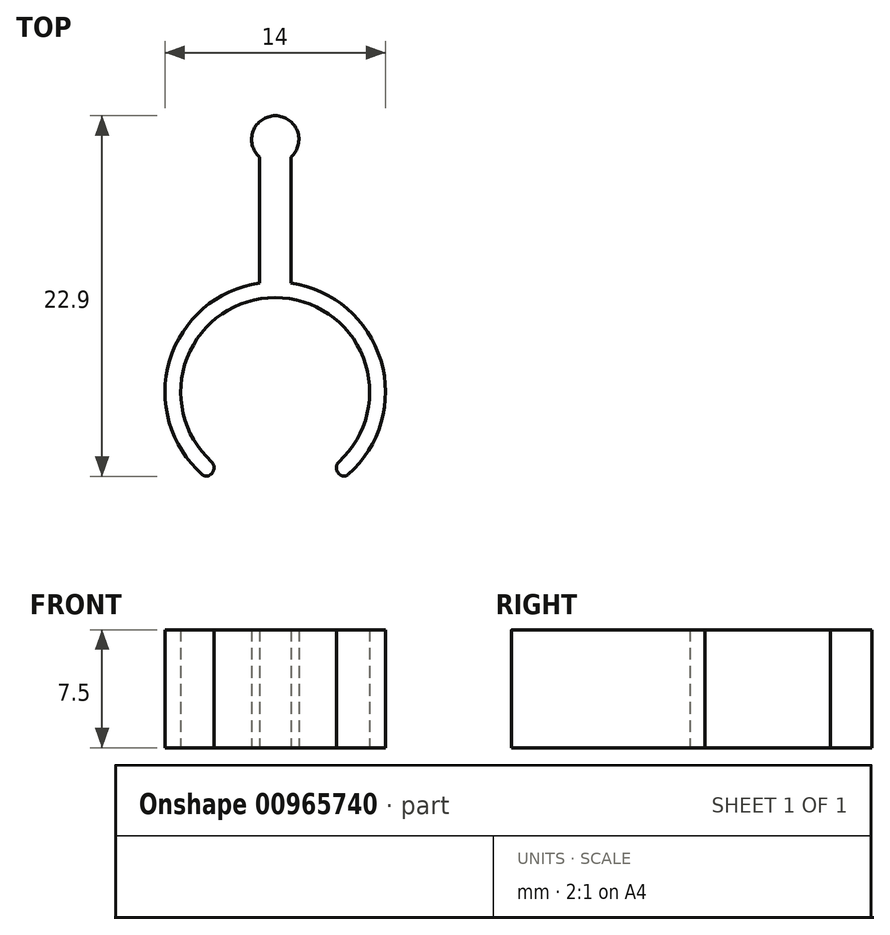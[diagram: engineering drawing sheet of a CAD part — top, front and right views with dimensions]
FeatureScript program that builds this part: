
annotation { "Feature Type Name" : "Feature", "Feature Type Description" : "" }
export const myFeature = defineFeature(function(context is Context, id is Id, definition is map)
    precondition{}
    {
        {
            var Q0;
            Q0=qCreatedBy(makeId("Top.planeOp"),FACE);
            var sketch = newSketch(context, id + "F0", { "sketchPlane" : qUnion([Q0])});
            skArc(sketch, "E0", {"start": v(4.64, -5.24) * mm, "mid": v(6.7, 2) * mm, "end": v(1, 6.93) * mm});
            skArc(sketch, "E1", {"start": v(4.05, -4.43) * mm, "mid": v(0, 6) * mm, "end": v(-4.05, -4.43) * mm});
            skLineSegment(sketch, "E2", {"start": v(3.99, -5.1) * mm, "end": v(4.06, -5.2) * mm});
            skLineSegment(sketch, "E3", {"start": v(-3.99, -5.1) * mm, "end": v(-4.06, -5.2) * mm});
            skLineSegment(sketch, "E4.left", {"start": v(1, 14.93) * mm, "end": v(1, 6.93) * mm});
            skLineSegment(sketch, "E4.right", {"start": v(-1, 14.93) * mm, "end": v(-1, 6.93) * mm});
            skArc(sketch, "E5.trimOffspring", {"start": v(-1, 6.93) * mm, "mid": v(-6.7, 2) * mm, "end": v(-4.64, -5.24) * mm});
            skArc(sketch, "E6", {"start": v(1, 14.93) * mm, "mid": v(0, 17.55) * mm, "end": v(-1, 14.93) * mm});
            skPoint(sketch, "E7.orphan", {"position": v(-1, 16.05) * mm});
            skPoint(sketch, "E8.orphan", {"position": v(1, 16.05) * mm});
            skPoint(sketch, "E9.visualSharp", {"position": v(-3.7, -4.73) * mm});
            skArc(sketch, "E9.filletArc", {"start": v(-3.99, -5.1) * mm, "mid": v(-3.89, -4.76) * mm, "end": v(-4.05, -4.43) * mm});
            skPoint(sketch, "E10.visualSharp", {"position": v(-4.3, -5.52) * mm});
            skArc(sketch, "E10.filletArc", {"start": v(-4.64, -5.24) * mm, "mid": v(-4.33, -5.34) * mm, "end": v(-4.06, -5.2) * mm});
            skPoint(sketch, "E11.visualSharp", {"position": v(3.7, -4.73) * mm});
            skArc(sketch, "E11.filletArc", {"start": v(4.05, -4.43) * mm, "mid": v(3.89, -4.76) * mm, "end": v(3.99, -5.1) * mm});
            skPoint(sketch, "E12.visualSharp", {"position": v(4.3, -5.52) * mm});
            skArc(sketch, "E12.filletArc", {"start": v(4.06, -5.2) * mm, "mid": v(4.33, -5.34) * mm, "end": v(4.64, -5.24) * mm});
            skSolve(sketch);
        }
        {
            var Q0;
            Q0=makeQuery(id+"F0.imprint","IMPRINT",FACE,{"disambiguationData":[TD([[makeQuery(id+"F0.imprint","IMPRINT",EDGE,{"derivedFrom":sQuery(id+"F0.wireOp",EDGE,"E0")}),1.0]])]});
            extrude(context, id + "F1", {"entities" : qUnion([Q0]), "depth" : 7.5 * mm, "offsetDistance" : 25 * mm});
        }
    });
